# Revit family: SLIM_FILUMO_20W_4000K_610MM
name_source: partatom
category: Lighting Fixtures
units: mm (PartAtom-declared; Revit-internal decimal feet)

## family parameters
Always vertical = Yes
Cut with Voids When Loaded = No
Host = Wall
Light Source = Yes
OmniClass Number = 23.80.70.00
OmniClass Title = Lighting
Part Type = Normal
Room Calculation Point = No
Round Connector Dimension = Use Diameter
Shared = No

## types (1)
- SLIM_FILUMO_20W_4000K_610MM
    Color Filter = 16777215
    Default Elevation = 0 mm  [stored 0 ft]
    Dimensions = 610 x 85 mm, Saillie : 45 mm
    Dimming Lamp Color Temperature Shift = <None>
    Driver = Driver Vossloh
    Durée de vie = 50 000 heures
    Emit from Line Length = 610 mm
    Fintion = Blanc laqué
    Light Source Symbol Size = 610 mm
    Puissance nominale = 20W
    Tension = AC 220-240V
    Type = Applique
    Type de lampe = LED SMD 2835

note: [stored X ft] marks values corroborated as IEEE doubles in the binary element streams (Revit-internal decimal feet)

## geometry (parser evidence)
native form markers: Sweep x3
no freeform markers — native parametric forms only
